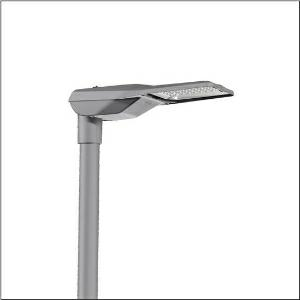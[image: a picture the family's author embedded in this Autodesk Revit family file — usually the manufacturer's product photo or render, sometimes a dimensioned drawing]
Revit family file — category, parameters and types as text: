
# Revit family: streetlight_sl_21_iq_mini___st1_0ab_5xe2m31v08gb_27e0
name_source: partatom
category: Lighting Fixtures
units: mm (PartAtom-declared; Revit-internal decimal feet)

## family parameters
Cut with Voids When Loaded = No
Host = Face
Light Source = No
Part Type = Normal
Room Calculation Point = No
Round Connector Dimension = Use Diameter
Shared = No

## types (1)
- --- (1 x LED, 5270 lm, 39.8 W, 3000K)
    Apparent Load = 40 VA
    CIE Flux Codes = 38 73 97 100 100
    Color Rendering = 70
    Color Temperature = 3000K
    Default Elevation = 1800 mm
    Description = Streetlight SL 21 iQ mini, mast luminaire, primary light control with lens, of PMMA, primary optical cover: cover, of toughened safety glass, transparent, light distribution: ST1.0aB, light emission: direct distribution, primary light characteristic: asymmetric, installation type: post-top, side-entry, LED, High Power LED, rated luminous flux: 5.270lm, luminous efficacy: 132lm/W, light colour: 730, colour temperature: 3000K, control gear: iQ-Street Remote, D4i with power reduction, control: pre-setting: logarithmic dimming characteristic, Street-Remote, Auto-Match, Temp-Guard, Lumen-Switch, Night-Set, Smart-Wire, Light-Fading, Desk-Remote (wireless, voltage-free reading and setting of iQ features in the workshop via application-optimized NFC function/RFID function), optimised constant luminous flux control (CLO 2.0), mains connection: 220..240V, AC, 50/60Hz, start of lifetime: 40W, end of service life: 41W, reduction: 18W, luminaire housing, of diecast aluminium, powder-coated, Siteco® metallic grey (DB 702S), corrosivity category C5 mid according to DIN EN ISO 12944, please order mast flange separately, inclination adjustable: 0°, 5°, 10°, 15°, sealing non-destructively replaceable, multi-level sealing system, length: 628mm, width: 235mm, height: 110mm, mast flange for spigot size: 42mm (side-entry): 5XC10008XM4, 60/48mm (side-entry/post-top): 5XC10108XM2, 76/60mm (side-entry/post-top): 5XC10108XM1, mounting height: 4..8m, Smart Interface above, protection rating (complete): IP66, insulation class (complete): insulation class II (safety insulation), certification: CE, ENEC, ENEC+, VDE, impact resistance: IK10, permissible operating ambient temperature for outdoor applications: -40..+50°C, standard-compliant lighting for roads and squares, packaging unit: 1 piece

Light Distribution: ST1.0aB
    Height = 110 mm
    Lamp = 1 x LED
    Lamp Light Flux = 5270 lm
    Lamp Power = 39.8 W
    Lamp count = 1
    Length = 625 mm
    Luminous efficacy = 132 lm/W
    Manufacturer = Siteco
    ModVariant = No
    Model = 5XE2M31V08GB
    Number of Poles = 1
    OnlyDefault = Yes
    Power Factor = 1
    Product Name = Streetlight SL 21 iQ mini | ST1.0aB
    Product group = mast luminaire | pylon top
    ProductGroupID = 6100
    Protection Class = Protection class II
    Protection Degree = IP 66
    RLX_Detail_Level = 1
    RLX_Emergency_Light_Flux = 0 lm
    RLX_Emergency_Type = 0
    RLX_Emergency_Type_DB = No
    RlxData = <blob elided: 26661 chars, md5=b9825d63>
    Socket = socket
    Standby Power = 0 W
    System Light Flux = 5270 lm
    System Power = 40 W
    Type Comments = factory setting: luminous flux: 100 % | dim-lin: 254 | 800 mA
    Type Image = l_1003515.jpg
    URL = http://relux.com
    VarID = @adj_112516
    Voltage = 0 V
    Weight = 0.00 kg
    Width = 234 mm

## geometry (parser evidence)
native form markers: Blend x4, Sweep x11
no freeform markers — native parametric forms only
